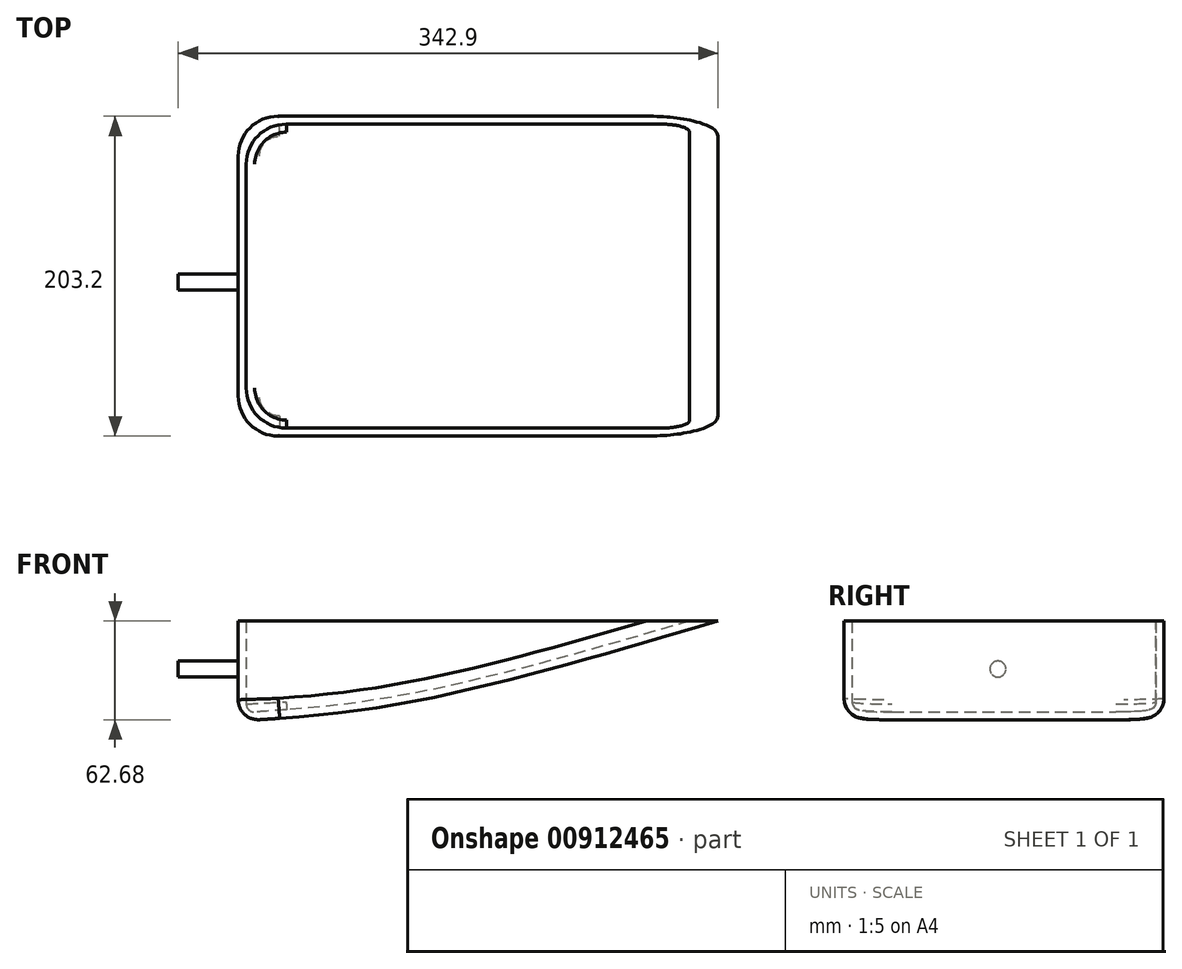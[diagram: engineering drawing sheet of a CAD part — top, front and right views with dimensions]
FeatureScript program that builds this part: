
annotation { "Feature Type Name" : "Feature", "Feature Type Description" : "" }
export const myFeature = defineFeature(function(context is Context, id is Id, definition is map)
    precondition{}
    {
        {
            var Q0;
            Q0=qCreatedBy(makeId("Front.planeOp"),FACE);
            var sketch = newSketch(context, id + "F0", { "sketchPlane" : qUnion([Q0])});
            skLineSegment(sketch, "E0.top", {"start": v(-149.5, -18.02) * mm, "end": v(155.3, -18.02) * mm});
            skLineSegment(sketch, "E1", {"start": v(-149.5, -18.02) * mm, "end": v(-149.5, -81.52) * mm});
            skFitSpline(sketch, "E2", {"points": [v(-149.5, -81.52) * mm, v(-42.85, -69.96) * mm, v(155.3, -18.02) * mm], "startDerivative": vector(235.64, 14.53) * mm, "endDerivative": vector(366.94, 107.5) * mm});
            skSolve(sketch);
        }
        {
            var Q0;
            Q0=makeQuery(id+"F0.imprint","IMPRINT",FACE,{"disambiguationData":[TD([[makeQuery(id+"F0.imprint","IMPRINT",EDGE,{"derivedFrom":sQuery(id+"F0.wireOp",EDGE,"E0.top")}),-1.0]])]});
            extrude(context, id + "F1", {"entities" : qUnion([Q0]), "depth" : 203.2 * mm, "offsetDistance" : 25.4 * mm});
        }
        {
            var Q0;
            Q0=makeQuery(id+"F1.opExtrude","SWEPT_FACE",FACE,{"disambiguationData":[OSD([sQuery(id+"F0.wireOp",EDGE,"E0.top")])]});
            shell(context, id + "F2", {"entities" : qUnion([Q0]), "thickness" : 5.08 * mm});
        }
        {
            var Q0;
            Q0=makeQuery(id+"F1.opExtrude","CAP_EDGE",EDGE,{"disambiguationData":[OSD([sQuery(id+"F0.wireOp",EDGE,"E1")])],"isStart":false});
            var Q1;
            {var subQ0=sQuery(id+"F0.wireOp",EDGE,"E1");Q1=makeQuery(id+"F2.opShell","OFFSET_EDGE",EDGE,{"disambiguationData":[OSD([subQ0]),TDD([makeQuery(id+"F1.opExtrude","CAP_EDGE",EDGE,{"disambiguationData":[OSD([subQ0])],"isStart":false})])]});}
            var Q2;
            {var subQ0=sQuery(id+"F0.wireOp",EDGE,"E1");Q2=makeQuery(id+"F2.opShell","OFFSET_EDGE",EDGE,{"disambiguationData":[OSD([subQ0]),TDD([makeQuery(id+"F1.opExtrude","CAP_EDGE",EDGE,{"disambiguationData":[OSD([subQ0])],"isStart":true})])]});}
            var Q3;
            Q3=makeQuery(id+"F1.opExtrude","CAP_EDGE",EDGE,{"disambiguationData":[OSD([sQuery(id+"F0.wireOp",EDGE,"E1")])],"isStart":true});
            fillet(context, id + "F3", {"entities" : qUnion([Q0, Q1, Q2, Q3]), "radius" : 25.4 * mm, "tangentPropagation" : true, "allowEdgeOverflow" : false});
        }
        {
            var Q0;
            Q0=makeQuery(id+"F1.opExtrude","SWEPT_FACE",FACE,{"disambiguationData":[OSD([sQuery(id+"F0.wireOp",EDGE,"E1")])]});
            var sketch = newSketch(context, id + "F4", { "sketchPlane" : qUnion([Q0])});
            skCircle(sketch, "E3", {"center": v(105.48, -48.5) * mm, "radius": 5.08 * mm});
            skSolve(sketch);
        }
        {
            var Q0;
            Q0 = qSketchRegion(id + "F4", true);
            extrude(context, id + "F5", {"entities" : qUnion([Q0]), "operationType" : NewBodyOperationType.ADD, "depth" : 38.1 * mm, "offsetDistance" : 25.4 * mm});
        }
        {
            var Q0;
            Q0=makeQuery(id+"F1.opExtrude","CAP_EDGE",EDGE,{"disambiguationData":[OSD([sQuery(id+"F0.wireOp",EDGE,"E2")])],"isStart":false});
            var Q1;
            Q1=makeQuery(id+"F1.opExtrude","CAP_EDGE",EDGE,{"disambiguationData":[OSD([sQuery(id+"F0.wireOp",EDGE,"E2")])],"isStart":true});
            fillet(context, id + "F6", {"entities" : qUnion([Q0, Q1]), "radius" : 12.7 * mm, "tangentPropagation" : true, "allowEdgeOverflow" : false});
        }
        {
            var Q0;
            {var subQ0=sQuery(id+"F0.wireOp",EDGE,"E2");Q0=makeQuery(id+"F2.opShell","OFFSET_EDGE",EDGE,{"disambiguationData":[OSD([subQ0]),TDD([makeQuery(id+"F1.opExtrude","CAP_EDGE",EDGE,{"disambiguationData":[OSD([subQ0])],"isStart":false})])]});}
            fillet(context, id + "F7", {"entities" : qUnion([Q0]), "radius" : 5.08 * mm, "tangentPropagation" : true, "allowEdgeOverflow" : false});
        }
    });
